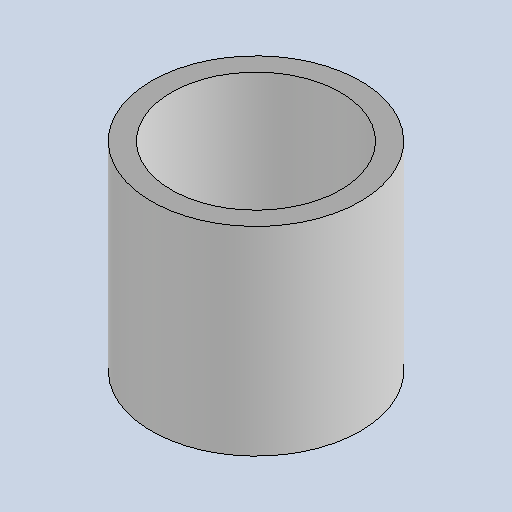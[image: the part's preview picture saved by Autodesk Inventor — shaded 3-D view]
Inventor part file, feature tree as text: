
AUTODESK INVENTOR PART (.ipt)
format: ipt  version: 2025.1 (Build 291241020, 241B)  size: 124,416 bytes
history: native  units: mm
features: extrude x1, sketch x1
ambient origin geometry x8: Origin, YZ Plane, XZ Plane, XY Plane, X Axis, Y Axis, Z Axis, Center Point
bodies: Body1 (feature_tree)
feature tree (2):
  extrude  "Extrusion5"  Depth=20.0mm
  sketch  "Sketch11"  dims[d187=21.0mm d188=2.0mm d189=20.0mm d190=0.0mm]
